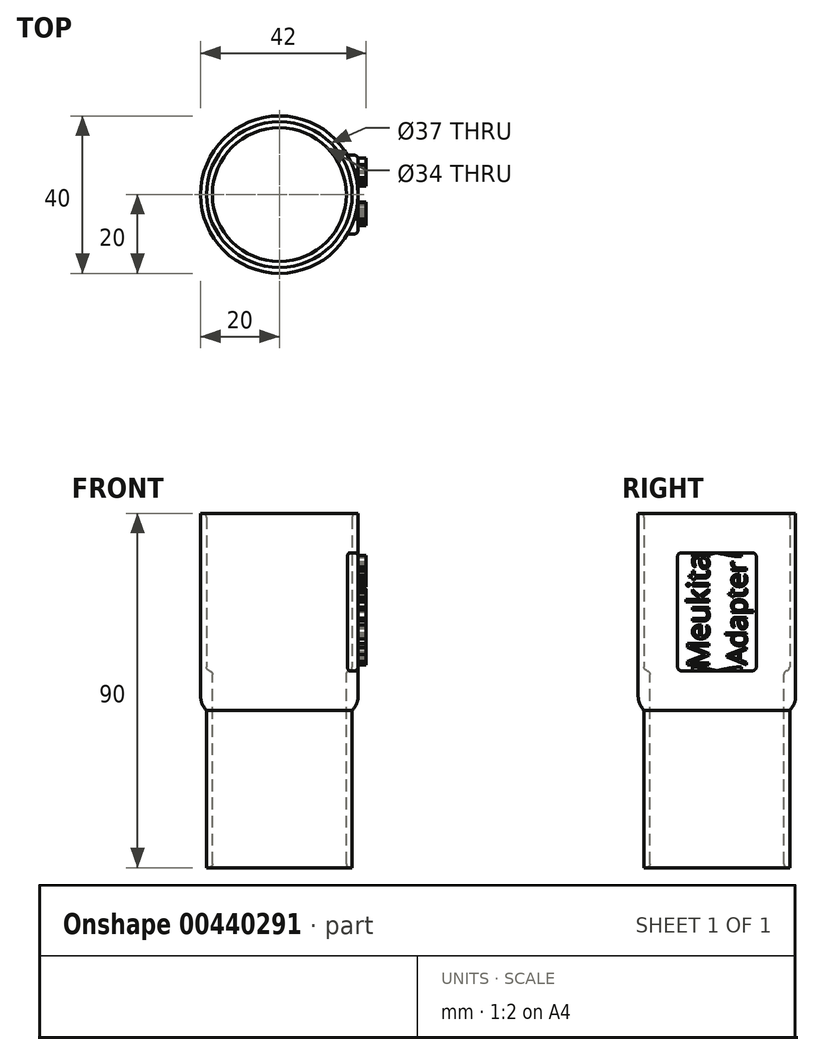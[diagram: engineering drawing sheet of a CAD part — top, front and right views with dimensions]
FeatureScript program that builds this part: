
annotation { "Feature Type Name" : "Feature", "Feature Type Description" : "" }
export const myFeature = defineFeature(function(context is Context, id is Id, definition is map)
    precondition{}
    {
        {
            var Q0;
            Q0=qCreatedBy(makeId("Top.planeOp"),FACE);
            var sketch = newSketch(context, id + "F0", { "sketchPlane" : qUnion([Q0])});
            skCircle(sketch, "E0", {"center": v(0, 0) * mm, "radius": 17 * mm});
            skCircle(sketch, "E1", {"center": v(0, 0) * mm, "radius": 18.5 * mm});
            skCircle(sketch, "E2", {"center": v(0, 0) * mm, "radius": 20 * mm});
            skSolve(sketch);
        }
        {
            var Q0;
            Q0 = qSketchRegion(id + "F0", true);
            extrude(context, id + "F1", {"entities" : qUnion([Q0]), "depth" : 40 * mm, "offsetDistance" : 25 * mm});
        }
        {
            var Q0;
            Q0=makeQuery(id+"F0.imprint","IMPRINT",FACE,{"disambiguationData":[TD([[makeQuery(id+"F0.imprint","IMPRINT",EDGE,{"derivedFrom":sQuery(id+"F0.wireOp",EDGE,"E1")}),-1.0]])]});
            extrude(context, id + "F2", {"entities" : qUnion([Q0]), "operationType" : NewBodyOperationType.ADD, "depth" : -10 * mm, "offsetDistance" : 25 * mm});
        }
        {
            var Q0;
            Q0=makeQuery(id+"F0.imprint","IMPRINT",FACE,{"disambiguationData":[TD([[makeQuery(id+"F0.imprint","IMPRINT",EDGE,{"derivedFrom":sQuery(id+"F0.wireOp",EDGE,"E0")}),-1.0]])]});
            extrude(context, id + "F3", {"entities" : qUnion([Q0]), "operationType" : NewBodyOperationType.ADD, "depth" : -50 * mm, "offsetDistance" : 25 * mm});
        }
        {
            var Q0;
            Q0=qCreatedBy(makeId("Top.planeOp"),FACE);
            var sketch = newSketch(context, id + "F4", { "sketchPlane" : qUnion([Q0])});
            skLineSegment(sketch, "E3", {"start": v(0, 0) * mm, "end": v(20, 0) * mm});
            skLineSegment(sketch, "E4", {"start": v(20, 0) * mm, "end": v(20, 10) * mm});
            skLineSegment(sketch, "E5", {"start": v(20, 10) * mm, "end": v(20, -10) * mm});
            skArc(sketch, "E6", {"start": v(17.32, -10) * mm, "mid": v(20, 0) * mm, "end": v(17.32, 10) * mm});
            skLineSegment(sketch, "E7", {"start": v(20, 10) * mm, "end": v(17.32, 10) * mm});
            skLineSegment(sketch, "E8", {"start": v(20, -10) * mm, "end": v(17.32, -10) * mm});
            skSolve(sketch);
        }
        {
            var Q0;
            {var subQ3=sQuery(id+"F4.wireOp",EDGE,"E8");Q0=makeQuery(id+"F4.imprint","IMPRINT",FACE,{"disambiguationData":[TD([[makeQuery(id+"F4.imprint","IMPRINT",EDGE,{"derivedFrom":subQ3}),-1.0]])]});}
            var Q1;
            {var subQ3=sQuery(id+"F4.wireOp",EDGE,"E7");Q1=makeQuery(id+"F4.imprint","IMPRINT",FACE,{"disambiguationData":[TD([[makeQuery(id+"F4.imprint","IMPRINT",EDGE,{"derivedFrom":subQ3}),1.0]])]});}
            extrude(context, id + "F5", {"entities" : qUnion([Q0, Q1]), "operationType" : NewBodyOperationType.ADD, "depth" : 30 * mm, "offsetDistance" : 25 * mm});
        }
        {
            var Q0;
            {var subQ0=sQuery(id+"F4.wireOp",EDGE,"E5");var subQ1=makeQuery(id+"F4.imprint","INTERSECT",VERTEX,{"derivedFrom":[subQ0,sQuery(id+"F4.wireOp",EDGE,"E6")]});Q0=makeQuery(id+"F5.boolean.opBoolean","MERGE",FACE,{"derivedFrom":[makeQuery(id+"F5.opExtrude","SWEPT_FACE",FACE,{"disambiguationData":[OSD([subQ0]),TDD([makeQuery(id+"F4.imprint","IMPRINT",EDGE,{"disambiguationData":[TD([[subQ1,1.0]])],"derivedFrom":subQ0})])]}),makeQuery(id+"F5.opExtrude","SWEPT_FACE",FACE,{"disambiguationData":[OSD([subQ0]),TDD([makeQuery(id+"F4.imprint","IMPRINT",EDGE,{"disambiguationData":[TD([[subQ1,-1.0]])],"derivedFrom":subQ0})])]})]});}
            var sketch = newSketch(context, id + "F6", { "sketchPlane" : qUnion([Q0])});
            skText(sketch, "E9", { "text": "Meukita", "fontName": "OpenSans-Regular.ttf"});
            skText(sketch, "E10", { "text": "Adapter", "fontName": "OpenSans-Regular.ttf"});
            const initialGuessF6  = {"E9": [-0.00199, 0.00068, 0, 1, 0.00559], "E10": [0.00756, 0.00153, 0, 1, 0.00506]};
            skSetInitialGuess(sketch, initialGuessF6);
            skSolve(sketch);
        }
        {
            var Q0;
            Q0 = qSketchRegion(id + "F6", true);
            extrude(context, id + "F7", {"entities" : qUnion([Q0]), "operationType" : NewBodyOperationType.ADD, "depth" : 2 * mm, "offsetDistance" : 25 * mm});
        }
        {
            var Q0;
            Q0=makeQuery(id+"F1.opExtrude","CAP_EDGE",EDGE,{"disambiguationData":[OSD([sQuery(id+"F0.wireOp",EDGE,"E1")])],"isStart":false});
            var Q1;
            {var subQ0=sQuery(id+"F0.wireOp",EDGE,"E1");Q1=makeQuery(id+"F2.boolean.opBoolean","MERGE",FACE,{"derivedFrom":[makeQuery(id+"F1.opExtrude","SWEPT_FACE",FACE,{"disambiguationData":[OSD([subQ0])]}),makeQuery(id+"F2.opExtrude","SWEPT_FACE",FACE,{"disambiguationData":[OSD([subQ0])]})]});}
            fillet(context, id + "F8", {"entities" : qUnion([Q0, Q1]), "radius" : 1 * mm, "tangentPropagation" : true, "allowEdgeOverflow" : false});
        }
        {
            var Q0;
            Q0=makeQuery(id+"F3.opExtrude","SWEPT_FACE",FACE,{"disambiguationData":[OSD([sQuery(id+"F0.wireOp",EDGE,"E0")])]});
            fillet(context, id + "F9", {"entities" : qUnion([Q0]), "radius" : 1 * mm, "tangentPropagation" : true, "allowEdgeOverflow" : false});
        }
        {
            var Q0;
            Q0=makeQuery(id+"F2.opExtrude","CAP_EDGE",EDGE,{"disambiguationData":[OSD([sQuery(id+"F0.wireOp",EDGE,"E2")])],"isStart":false});
            fillet(context, id + "F10", {"entities" : qUnion([Q0]), "radius" : 5 * mm, "tangentPropagation" : true, "allowEdgeOverflow" : false});
        }
        {
            var Q0;
            Q0=makeQuery(id+"F5.opExtrude","SWEPT_EDGE",EDGE,{"disambiguationData":[OSD([sQuery(id+"F4.wireOp",EDGE,"E6"),sQuery(id+"F4.wireOp",EDGE,"E7")])]});
            var Q1;
            {var subQ0=sQuery(id+"F4.wireOp",EDGE,"E6");Q1=makeQuery(id+"F5.opExtrude","CAP_EDGE",EDGE,{"disambiguationData":[OSD([subQ0]),TDD([makeQuery(id+"F4.imprint","IMPRINT",EDGE,{"disambiguationData":[TD([[makeQuery(id+"F4.imprint","INTERSECT",VERTEX,{"derivedFrom":[sQuery(id+"F4.wireOp",EDGE,"E5"),subQ0]}),-1.0]])],"derivedFrom":subQ0})])],"isStart":true});}
            var Q2;
            {var subQ0=sQuery(id+"F4.wireOp",EDGE,"E6");Q2=makeQuery(id+"F5.opExtrude","CAP_EDGE",EDGE,{"disambiguationData":[OSD([subQ0]),TDD([makeQuery(id+"F4.imprint","IMPRINT",EDGE,{"disambiguationData":[TD([[makeQuery(id+"F4.imprint","INTERSECT",VERTEX,{"derivedFrom":[sQuery(id+"F4.wireOp",EDGE,"E5"),subQ0]}),-1.0]])],"derivedFrom":subQ0})])],"isStart":false});}
            var Q3;
            Q3=makeQuery(id+"F5.opExtrude","SWEPT_EDGE",EDGE,{"disambiguationData":[OSD([sQuery(id+"F4.wireOp",EDGE,"E6"),sQuery(id+"F4.wireOp",EDGE,"E8")])]});
            var Q4;
            Q4=makeQuery(id+"F5.opExtrude","SWEPT_EDGE",EDGE,{"disambiguationData":[OSD([sQuery(id+"F4.wireOp",EDGE,"E5"),sQuery(id+"F4.wireOp",EDGE,"E8")])]});
            var Q5;
            Q5=makeQuery(id+"F5.opExtrude","SWEPT_EDGE",EDGE,{"disambiguationData":[OSD([sQuery(id+"F4.wireOp",EDGE,"E5"),sQuery(id+"F4.wireOp",EDGE,"E7")])]});
            fillet(context, id + "F11", {"entities" : qUnion([Q0, Q1, Q2, Q3, Q4, Q5]), "radius" : 1 * mm, "tangentPropagation" : true, "allowEdgeOverflow" : false});
        }
        {
            var Q0;
            {var subQ0=sQuery(id+"F4.wireOp",EDGE,"E8");var subQ1=sQuery(id+"F4.wireOp",EDGE,"E5");Q0=makeQuery(id+"F11.opFillet","BLEND_EDGE",EDGE,{"blendedFrom":[makeQuery(id+"F5.opExtrude","SWEPT_EDGE",EDGE,{"disambiguationData":[OSD([subQ1,subQ0])]}),makeQuery(id+"F5.opExtrude","CAP_FACE",FACE,{"disambiguationData":[OSD([subQ1,sQuery(id+"F4.wireOp",EDGE,"E6"),subQ0])],"isStart":false})],"blendedInto":[makeQuery(id+"F5.opExtrude","CAP_FACE",FACE,{"disambiguationData":[OSD([subQ1,sQuery(id+"F4.wireOp",EDGE,"E6"),subQ0])],"isStart":false})]});}
            var Q1;
            {var subQ0=sQuery(id+"F4.wireOp",EDGE,"E8");var subQ1=sQuery(id+"F4.wireOp",EDGE,"E5");Q1=makeQuery(id+"F11.opFillet","BLEND_EDGE",EDGE,{"blendedFrom":[makeQuery(id+"F5.opExtrude","SWEPT_EDGE",EDGE,{"disambiguationData":[OSD([subQ1,subQ0])]}),makeQuery(id+"F5.opExtrude","CAP_FACE",FACE,{"disambiguationData":[OSD([subQ1,sQuery(id+"F4.wireOp",EDGE,"E6"),subQ0])],"isStart":true})],"blendedInto":[makeQuery(id+"F5.opExtrude","CAP_FACE",FACE,{"disambiguationData":[OSD([subQ1,sQuery(id+"F4.wireOp",EDGE,"E6"),subQ0])],"isStart":true})]});}
            var Q2;
            {var subQ0=sQuery(id+"F4.wireOp",EDGE,"E7");var subQ1=sQuery(id+"F4.wireOp",EDGE,"E5");Q2=makeQuery(id+"F11.opFillet","BLEND_EDGE",EDGE,{"blendedFrom":[makeQuery(id+"F5.opExtrude","SWEPT_EDGE",EDGE,{"disambiguationData":[OSD([subQ1,subQ0])]}),makeQuery(id+"F5.opExtrude","CAP_FACE",FACE,{"disambiguationData":[OSD([subQ1,sQuery(id+"F4.wireOp",EDGE,"E6"),subQ0])],"isStart":true})],"blendedInto":[makeQuery(id+"F5.opExtrude","CAP_FACE",FACE,{"disambiguationData":[OSD([subQ1,sQuery(id+"F4.wireOp",EDGE,"E6"),subQ0])],"isStart":true})]});}
            var Q3;
            {var subQ0=sQuery(id+"F4.wireOp",EDGE,"E7");var subQ1=sQuery(id+"F4.wireOp",EDGE,"E5");Q3=makeQuery(id+"F11.opFillet","BLEND_EDGE",EDGE,{"blendedFrom":[makeQuery(id+"F5.opExtrude","SWEPT_EDGE",EDGE,{"disambiguationData":[OSD([subQ1,subQ0])]}),makeQuery(id+"F5.opExtrude","CAP_FACE",FACE,{"disambiguationData":[OSD([subQ1,sQuery(id+"F4.wireOp",EDGE,"E6"),subQ0])],"isStart":false})],"blendedInto":[makeQuery(id+"F5.opExtrude","CAP_FACE",FACE,{"disambiguationData":[OSD([subQ1,sQuery(id+"F4.wireOp",EDGE,"E6"),subQ0])],"isStart":false})]});}
            fillet(context, id + "F12", {"entities" : qUnion([Q0, Q1, Q2, Q3]), "radius" : 1 * mm, "tangentPropagation" : true, "allowEdgeOverflow" : false});
        }
    });
